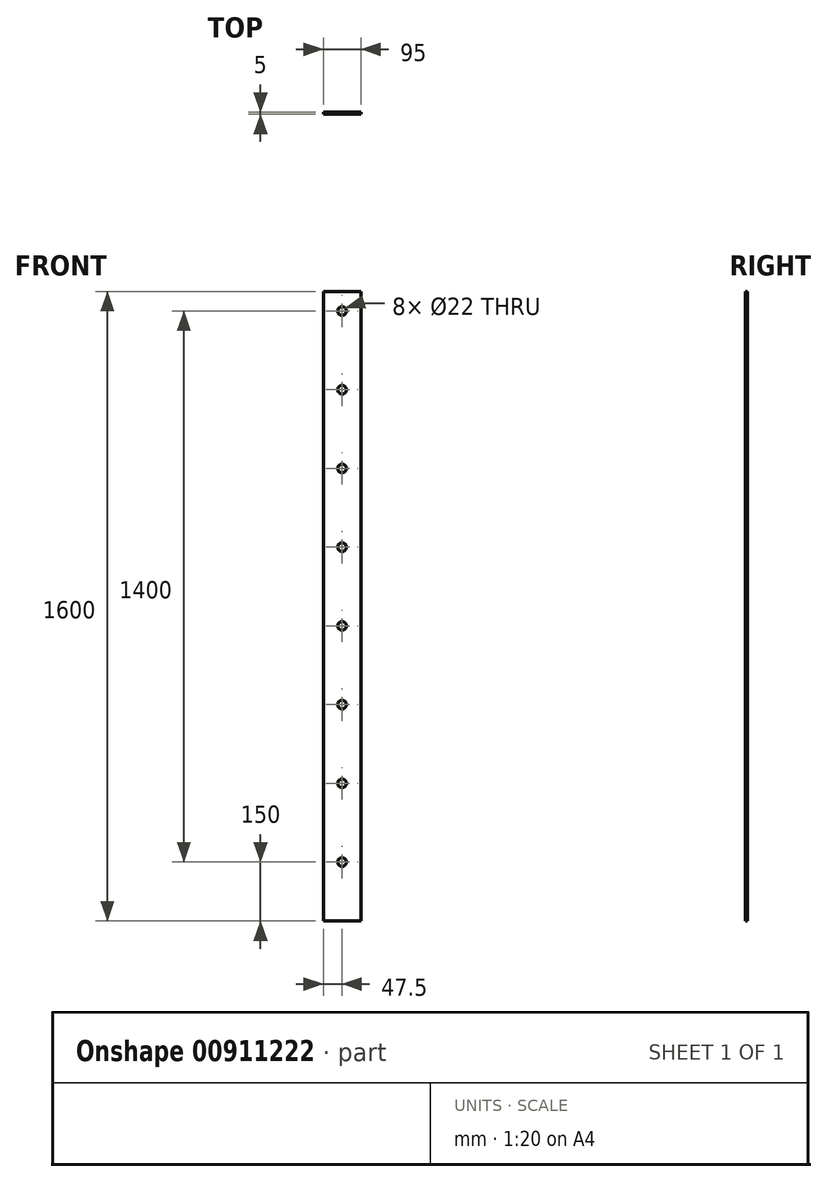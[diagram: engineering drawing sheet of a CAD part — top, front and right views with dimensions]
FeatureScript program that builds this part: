
annotation { "Feature Type Name" : "Feature", "Feature Type Description" : "" }
export const myFeature = defineFeature(function(context is Context, id is Id, definition is map)
    precondition{}
    {
        {
            var Q0;
            Q0=qCreatedBy(makeId("Front.planeOp"),FACE);
            var sketch = newSketch(context, id + "F0", { "sketchPlane" : qUnion([Q0])});
            skLineSegment(sketch, "E0.bottom", {"start": v(47.5, 800) * mm, "end": v(-47.5, 800) * mm});
            skLineSegment(sketch, "E0.top", {"start": v(47.5, -800) * mm, "end": v(-47.5, -800) * mm});
            skLineSegment(sketch, "E0.left", {"start": v(47.5, 800) * mm, "end": v(47.5, -800) * mm});
            skLineSegment(sketch, "E0.right", {"start": v(-47.5, 800) * mm, "end": v(-47.5, -800) * mm});
            skPoint(sketch, "E0.middle", {"position": v(0, 0) * mm});
            skSolve(sketch);
        }
        {
            var Q0;
            Q0=makeQuery(id+"F0.imprint","IMPRINT",FACE,{"disambiguationData":[TD([[makeQuery(id+"F0.imprint","IMPRINT",EDGE,{"derivedFrom":sQuery(id+"F0.wireOp",EDGE,"E0.bottom")}),1.0]])]});
            extrude(context, id + "F1", {"entities" : qUnion([Q0]), "depth" : 5 * mm, "offsetDistance" : 25 * mm});
        }
        {
            var Q0;
            Q0=makeQuery(id+"F1.opExtrude","CAP_FACE",FACE,{"disambiguationData":[OSD([sQuery(id+"F0.wireOp",EDGE,"E0.bottom"),sQuery(id+"F0.wireOp",EDGE,"E0.top"),sQuery(id+"F0.wireOp",EDGE,"E0.left"),sQuery(id+"F0.wireOp",EDGE,"E0.right")])],"isStart":false});
            var sketch = newSketch(context, id + "F2", { "sketchPlane" : qUnion([Q0])});
            skCircle(sketch, "E1", {"center": v(0, 750) * mm, "radius": 11 * mm});
            skCircle(sketch, "E2", {"center": v(0, 550) * mm, "radius": 11 * mm});
            skCircle(sketch, "E3", {"center": v(0, 350) * mm, "radius": 11 * mm});
            skCircle(sketch, "E4", {"center": v(0, 150) * mm, "radius": 11 * mm});
            skCircle(sketch, "E5", {"center": v(0, -50) * mm, "radius": 11 * mm});
            skCircle(sketch, "E6", {"center": v(0, -250) * mm, "radius": 11 * mm});
            skCircle(sketch, "E7", {"center": v(0, -450) * mm, "radius": 11 * mm});
            skCircle(sketch, "E8", {"center": v(0, -650) * mm, "radius": 11 * mm});
            skSolve(sketch);
        }
        {
            var Q0;
            Q0=makeQuery(id+"F2.imprint","IMPRINT",FACE,{"disambiguationData":[TD([[makeQuery(id+"F2.imprint","IMPRINT",EDGE,{"derivedFrom":sQuery(id+"F2.wireOp",EDGE,"E6")}),1.0]])]});
            var Q1;
            Q1=makeQuery(id+"F2.imprint","IMPRINT",FACE,{"disambiguationData":[TD([[makeQuery(id+"F2.imprint","IMPRINT",EDGE,{"derivedFrom":sQuery(id+"F2.wireOp",EDGE,"E5")}),1.0]])]});
            var Q2;
            Q2=makeQuery(id+"F2.imprint","IMPRINT",FACE,{"disambiguationData":[TD([[makeQuery(id+"F2.imprint","IMPRINT",EDGE,{"derivedFrom":sQuery(id+"F2.wireOp",EDGE,"E4")}),1.0]])]});
            var Q3;
            Q3=makeQuery(id+"F2.imprint","IMPRINT",FACE,{"disambiguationData":[TD([[makeQuery(id+"F2.imprint","IMPRINT",EDGE,{"derivedFrom":sQuery(id+"F2.wireOp",EDGE,"E3")}),1.0]])]});
            var Q4;
            Q4=makeQuery(id+"F2.imprint","IMPRINT",FACE,{"disambiguationData":[TD([[makeQuery(id+"F2.imprint","IMPRINT",EDGE,{"derivedFrom":sQuery(id+"F2.wireOp",EDGE,"E2")}),1.0]])]});
            var Q5;
            Q5=makeQuery(id+"F2.imprint","IMPRINT",FACE,{"disambiguationData":[TD([[makeQuery(id+"F2.imprint","IMPRINT",EDGE,{"derivedFrom":sQuery(id+"F2.wireOp",EDGE,"E1")}),1.0]])]});
            var Q6;
            Q6=makeQuery(id+"F2.imprint","IMPRINT",FACE,{"disambiguationData":[TD([[makeQuery(id+"F2.imprint","IMPRINT",EDGE,{"derivedFrom":sQuery(id+"F2.wireOp",EDGE,"E7")}),1.0]])]});
            var Q7;
            Q7=makeQuery(id+"F2.imprint","IMPRINT",FACE,{"disambiguationData":[TD([[makeQuery(id+"F2.imprint","IMPRINT",EDGE,{"derivedFrom":sQuery(id+"F2.wireOp",EDGE,"E8")}),1.0]])]});
            extrude(context, id + "F3", {"entities" : qUnion([Q0, Q1, Q2, Q3, Q4, Q5, Q6, Q7]), "operationType" : NewBodyOperationType.REMOVE, "oppositeDirection" : true, "depth" : 25 * mm, "offsetDistance" : 25 * mm});
        }
    });
